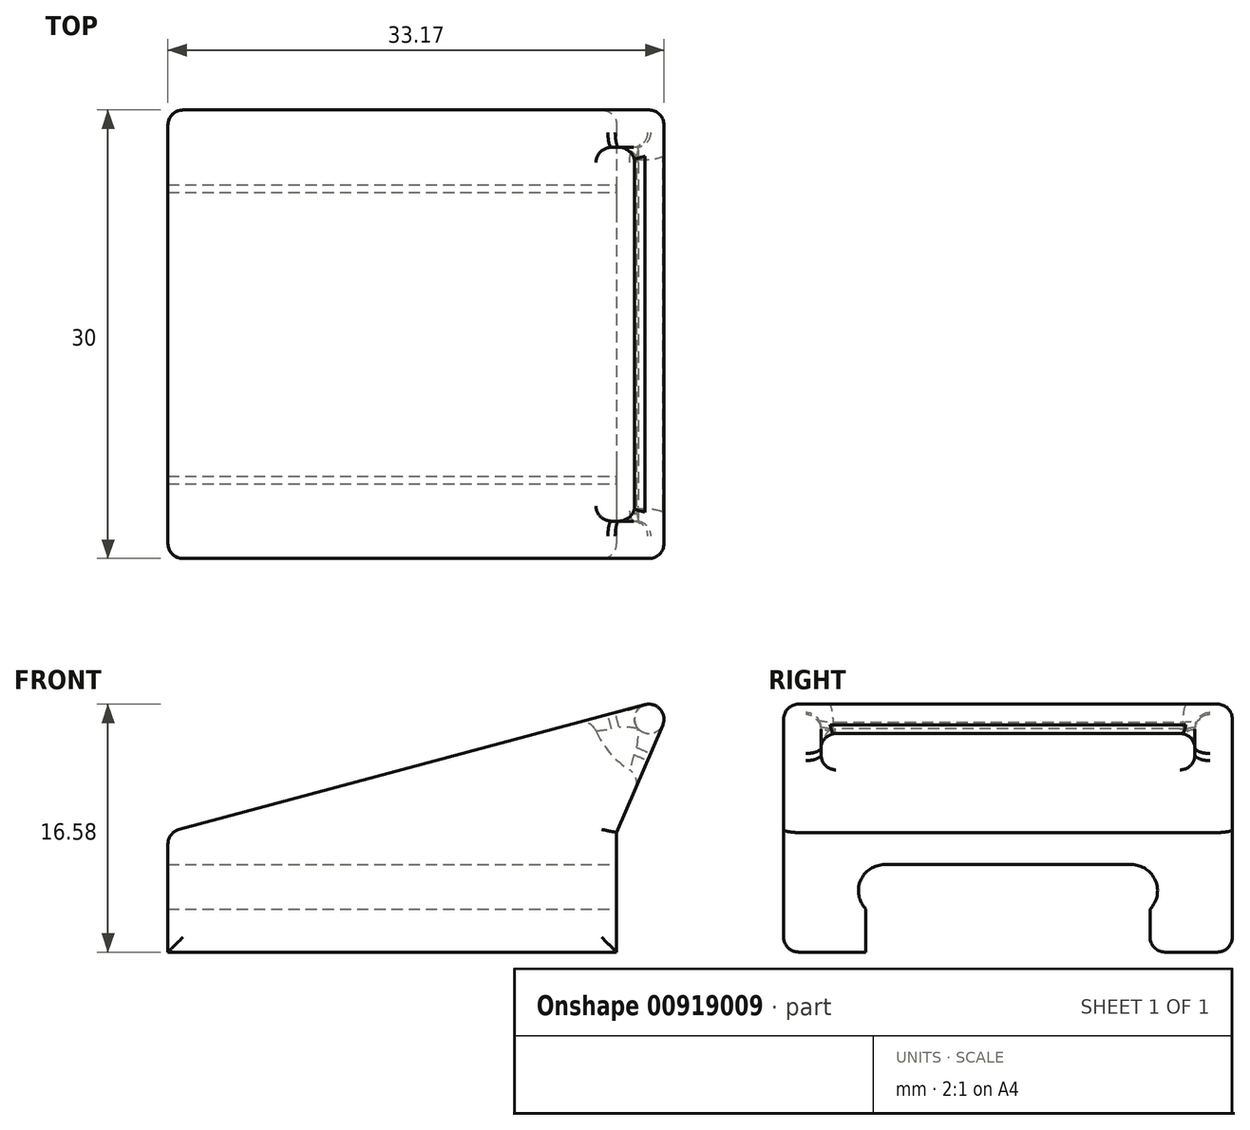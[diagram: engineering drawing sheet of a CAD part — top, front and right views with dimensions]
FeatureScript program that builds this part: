
annotation { "Feature Type Name" : "Feature", "Feature Type Description" : "" }
export const myFeature = defineFeature(function(context is Context, id is Id, definition is map)
    precondition{}
    {
        {
            var Q0;
            Q0=qCreatedBy(makeId("Top.planeOp"),FACE);
            var sketch = newSketch(context, id + "F0", { "sketchPlane" : qUnion([Q0])});
            skLineSegment(sketch, "E0.bottom", {"start": v(15, 15) * mm, "end": v(-15, 15) * mm});
            skLineSegment(sketch, "E0.top", {"start": v(15, -15) * mm, "end": v(-15, -15) * mm});
            skLineSegment(sketch, "E0.left", {"start": v(15, 15) * mm, "end": v(15, -15) * mm});
            skLineSegment(sketch, "E0.right", {"start": v(-15, 15) * mm, "end": v(-15, -15) * mm});
            skPoint(sketch, "E0.middle", {"position": v(0, 0) * mm});
            skSolve(sketch);
        }
        {
            var Q0;
            Q0=makeQuery(id+"F0.imprint","IMPRINT",FACE,{"disambiguationData":[TD([[makeQuery(id+"F0.imprint","IMPRINT",EDGE,{"derivedFrom":sQuery(id+"F0.wireOp",EDGE,"E0.bottom")}),1.0]])]});
            extrude(context, id + "F1", {"entities" : qUnion([Q0]), "oppositeDirection" : true, "depth" : 8 * mm, "offsetDistance" : 25 * mm});
        }
        {
            var Q0;
            Q0=makeQuery(id+"F1.opExtrude","SWEPT_FACE",FACE,{"disambiguationData":[OSD([sQuery(id+"F0.wireOp",EDGE,"E0.left")])]});
            var sketch = newSketch(context, id + "F2", { "sketchPlane" : qUnion([Q0])});
            skLineSegment(sketch, "E1", {"start": v(0, 9) * mm, "end": v(0, -16.8) * mm, "construction": true});
            skPoint(sketch, "E1.startSnap0", {"position": v(0, 0) * mm});
            skLineSegment(sketch, "E2.bottom", {"start": v(8.25, -2.15) * mm, "end": v(-8.25, -2.15) * mm});
            skLineSegment(sketch, "E2.left", {"start": v(10, -3.9) * mm, "end": v(10, -3.9) * mm});
            skLineSegment(sketch, "E2.right", {"start": v(-10, -3.9) * mm, "end": v(-10, -3.9) * mm});
            skPoint(sketch, "E2.middle", {"position": v(0, -3.9) * mm});
            skPoint(sketch, "E3.visualSharp", {"position": v(-10, -2.15) * mm});
            skArc(sketch, "E3.filletArc", {"start": v(-8.25, -2.15) * mm, "mid": v(-9.49, -2.66) * mm, "end": v(-10, -3.9) * mm});
            skPoint(sketch, "E4.visualSharp", {"position": v(-10, -5.65) * mm});
            skArc(sketch, "E4.filletArc", {"start": v(-10, -3.9) * mm, "mid": v(-9.87, -4.56) * mm, "end": v(-9.5, -5.12) * mm});
            skPoint(sketch, "E5.visualSharp", {"position": v(10, -5.65) * mm});
            skArc(sketch, "E5.filletArc", {"start": v(9.5, -5.12) * mm, "mid": v(9.87, -4.56) * mm, "end": v(10, -3.9) * mm});
            skPoint(sketch, "E6.visualSharp", {"position": v(10, -2.15) * mm});
            skArc(sketch, "E6.filletArc", {"start": v(10, -3.9) * mm, "mid": v(9.49, -2.66) * mm, "end": v(8.25, -2.15) * mm});
            skLineSegment(sketch, "E7", {"start": v(-9.5, -5.12) * mm, "end": v(-9.5, -8) * mm});
            skLineSegment(sketch, "E8", {"start": v(-9.5, -8) * mm, "end": v(9.5, -8) * mm});
            skLineSegment(sketch, "E9", {"start": v(9.5, -8) * mm, "end": v(9.5, -5.12) * mm});
            skSolve(sketch);
        }
        {
            var Q0;
            Q0=makeQuery(id+"F2.imprint","IMPRINT",FACE,{"disambiguationData":[TD([[makeQuery(id+"F2.imprint","IMPRINT",EDGE,{"derivedFrom":sQuery(id+"F2.wireOp",EDGE,"E2.bottom")}),1.0]])]});
            extrude(context, id + "F3", {"entities" : qUnion([Q0]), "operationType" : NewBodyOperationType.REMOVE, "endBound" : BoundingType.THROUGH_ALL, "oppositeDirection" : true, "depth" : 25 * mm, "offsetDistance" : 25 * mm});
        }
        {
            var Q0;
            Q0=makeQuery(id+"F1.opExtrude","SWEPT_FACE",FACE,{"disambiguationData":[OSD([sQuery(id+"F0.wireOp",EDGE,"E0.bottom")])]});
            var sketch = newSketch(context, id + "F4", { "sketchPlane" : qUnion([Q0])});
            skLineSegment(sketch, "E10.0", {"start": v(-15, 0) * mm, "end": v(15, 0) * mm});
            skLineSegment(sketch, "E11", {"start": v(-15, 0) * mm, "end": v(-18.9, 9.08) * mm});
            skLineSegment(sketch, "E12", {"start": v(-18.9, 9.08) * mm, "end": v(15, 0) * mm});
            skSolve(sketch);
        }
        {
            var Q0;
            Q0=makeQuery(id+"F4.imprint","IMPRINT",FACE,{"disambiguationData":[TD([[makeQuery(id+"F4.imprint","IMPRINT",EDGE,{"derivedFrom":sQuery(id+"F4.wireOp",EDGE,"E10.0")}),1.0]])]});
            extrude(context, id + "F5", {"entities" : qUnion([Q0]), "operationType" : NewBodyOperationType.ADD, "oppositeDirection" : true, "depth" : 30 * mm, "offsetDistance" : 25 * mm});
        }
        {
            var Q0;
            Q0=makeQuery(id+"F5.opExtrude","SWEPT_FACE",FACE,{"disambiguationData":[OSD([sQuery(id+"F4.wireOp",EDGE,"E11")])]});
            var sketch = newSketch(context, id + "F6", { "sketchPlane" : qUnion([Q0])});
            skLineSegment(sketch, "E13.bottom", {"start": v(11.5, 12.55) * mm, "end": v(-11.5, 12.55) * mm});
            skLineSegment(sketch, "E13.top", {"start": v(11.5, 10.05) * mm, "end": v(-11.5, 10.05) * mm});
            skLineSegment(sketch, "E13.left", {"start": v(12.5, 11.55) * mm, "end": v(12.5, 11.05) * mm});
            skLineSegment(sketch, "E13.right", {"start": v(-12.5, 11.55) * mm, "end": v(-12.5, 11.05) * mm});
            skPoint(sketch, "E13.middle", {"position": v(0, 11.3) * mm});
            skPoint(sketch, "E13.middle.positionSnap0", {"position": v(0, 15.8) * mm});
            skPoint(sketch, "E13.centerSnap0", {"position": v(0, 15.8) * mm});
            skPoint(sketch, "E14.visualSharp", {"position": v(-12.5, 12.55) * mm});
            skArc(sketch, "E14.filletArc", {"start": v(-11.5, 12.55) * mm, "mid": v(-12.2, 12.26) * mm, "end": v(-12.5, 11.55) * mm});
            skPoint(sketch, "E15.visualSharp", {"position": v(-12.5, 10.05) * mm});
            skArc(sketch, "E15.filletArc", {"start": v(-12.5, 11.05) * mm, "mid": v(-12.2, 10.34) * mm, "end": v(-11.5, 10.05) * mm});
            skPoint(sketch, "E16.visualSharp", {"position": v(12.5, 10.05) * mm});
            skArc(sketch, "E16.filletArc", {"start": v(11.5, 10.05) * mm, "mid": v(12.2, 10.34) * mm, "end": v(12.5, 11.05) * mm});
            skPoint(sketch, "E17.visualSharp", {"position": v(12.5, 12.55) * mm});
            skArc(sketch, "E17.filletArc", {"start": v(12.5, 11.55) * mm, "mid": v(12.2, 12.26) * mm, "end": v(11.5, 12.55) * mm});
            skSolve(sketch);
        }
        {
            var Q0;
            Q0=makeQuery(id+"F6.imprint","IMPRINT",FACE,{"disambiguationData":[TD([[makeQuery(id+"F6.imprint","IMPRINT",EDGE,{"derivedFrom":sQuery(id+"F6.wireOp",EDGE,"E13.bottom")}),1.0]])]});
            var Q1;
            Q1=makeQuery(id+"F5.opExtrude","SWEPT_EDGE",EDGE,{"disambiguationData":[OSD([sQuery(id+"F4.wireOp",EDGE,"E11"),sQuery(id+"F4.wireOp",EDGE,"E12")])]});
            revolve(context, id + "F7", {"operationType" : NewBodyOperationType.REMOVE, "surfaceOperationType" : NewSurfaceOperationType.NEW, "entities" : qUnion([Q0]), "axis" : qUnion([Q1]), "revolveType" : RevolveType.FULL, "oppositeDirection" : true});
        }
        {
            var Q0;
            Q0=makeQuery(id+"F5.opExtrude","SWEPT_EDGE",EDGE,{"disambiguationData":[OSD([sQuery(id+"F4.wireOp",EDGE,"E11"),sQuery(id+"F4.wireOp",EDGE,"E12")])]});
            var Q1;
            Q1=makeQuery(id+"F5.opExtrude","CAP_EDGE",EDGE,{"disambiguationData":[OSD([sQuery(id+"F4.wireOp",EDGE,"E12")])],"isStart":true});
            var Q2;
            Q2=makeQuery(id+"F5.opExtrude","CAP_EDGE",EDGE,{"disambiguationData":[OSD([sQuery(id+"F4.wireOp",EDGE,"E12")])],"isStart":false});
            var Q3;
            Q3=makeQuery(id+"F5.opExtrude","CAP_EDGE",EDGE,{"disambiguationData":[OSD([sQuery(id+"F4.wireOp",EDGE,"E11")])],"isStart":true});
            var Q4;
            Q4=makeQuery(id+"F1.opExtrude","SWEPT_EDGE",EDGE,{"disambiguationData":[OSD([sQuery(id+"F0.wireOp",EDGE,"E0.bottom"),sQuery(id+"F0.wireOp",EDGE,"E0.left")])]});
            var Q5;
            Q5=makeQuery(id+"F1.opExtrude","SWEPT_EDGE",EDGE,{"disambiguationData":[OSD([sQuery(id+"F0.wireOp",EDGE,"E0.top"),sQuery(id+"F0.wireOp",EDGE,"E0.left")])]});
            var Q6;
            Q6=makeQuery(id+"F5.opExtrude","CAP_EDGE",EDGE,{"disambiguationData":[OSD([sQuery(id+"F4.wireOp",EDGE,"E11")])],"isStart":false});
            var Q7;
            Q7=makeQuery(id+"F1.opExtrude","SWEPT_EDGE",EDGE,{"disambiguationData":[OSD([sQuery(id+"F0.wireOp",EDGE,"E0.top"),sQuery(id+"F0.wireOp",EDGE,"E0.right")])]});
            var Q8;
            Q8=makeQuery(id+"F1.opExtrude","SWEPT_EDGE",EDGE,{"disambiguationData":[OSD([sQuery(id+"F0.wireOp",EDGE,"E0.bottom"),sQuery(id+"F0.wireOp",EDGE,"E0.right")])]});
            var Q9;
            {var subQ0=sQuery(id+"F0.wireOp",EDGE,"E0.right");Q9=makeQuery(id+"F5.boolean.opBoolean","MERGE",EDGE,{"derivedFrom":[makeQuery(id+"F1.opExtrude","CAP_EDGE",EDGE,{"disambiguationData":[OSD([subQ0])],"isStart":true}),makeQuery(id+"F5.opExtrude","SWEPT_EDGE",EDGE,{"disambiguationData":[OSD([sQuery(id+"F0.wireOp",EDGE,"E0.bottom"),subQ0,sQuery(id+"F4.wireOp",EDGE,"E10.0"),sQuery(id+"F4.wireOp",EDGE,"E12")])]})]});}
            var Q10;
            Q10=makeQuery(id+"F3.boolean.opBoolean","COPY",EDGE,{"derivedFrom":makeQuery(id+"F3.opExtrude","SWEPT_EDGE",EDGE,{"disambiguationData":[OSD([sQuery(id+"F0.wireOp",EDGE,"E0.left"),sQuery(id+"F2.wireOp",EDGE,"E7"),sQuery(id+"F2.wireOp",EDGE,"E8")])]})});
            var Q11;
            Q11=makeQuery(id+"F3.boolean.opBoolean","COPY",EDGE,{"derivedFrom":makeQuery(id+"F3.opExtrude","SWEPT_EDGE",EDGE,{"disambiguationData":[OSD([sQuery(id+"F0.wireOp",EDGE,"E0.left"),sQuery(id+"F2.wireOp",EDGE,"E8"),sQuery(id+"F2.wireOp",EDGE,"E9")])]})});
            var Q12;
            Q12=makeQuery(id+"F1.opExtrude","CAP_EDGE",EDGE,{"disambiguationData":[OSD([sQuery(id+"F0.wireOp",EDGE,"E0.top")])],"isStart":false});
            var Q13;
            Q13=makeQuery(id+"F1.opExtrude","CAP_EDGE",EDGE,{"disambiguationData":[OSD([sQuery(id+"F0.wireOp",EDGE,"E0.bottom")])],"isStart":false});
            fillet(context, id + "F8", {"entities" : qUnion([Q0, Q1, Q2, Q3, Q4, Q5, Q6, Q7, Q8, Q9, Q10, Q11, Q12, Q13]), "radius" : 1 * mm, "tangentPropagation" : true, "allowEdgeOverflow" : false});
        }
        {
            var Q0;
            Q0=makeQuery(id+"F7.boolean.opBoolean","INTERSECT",EDGE,{"derivedFrom":[makeQuery(id+"F5.opExtrude","SWEPT_FACE",FACE,{"disambiguationData":[OSD([sQuery(id+"F4.wireOp",EDGE,"E12")])]}),makeQuery(id+"F7.opRevolve","SWEPT_FACE",FACE,{"disambiguationData":[OSD([sQuery(id+"F6.wireOp",EDGE,"E13.top")])]})]});
            var Q1;
            Q1=makeQuery(id+"F7.boolean.opBoolean","INTERSECT",EDGE,{"derivedFrom":[makeQuery(id+"F5.opExtrude","SWEPT_FACE",FACE,{"disambiguationData":[OSD([sQuery(id+"F4.wireOp",EDGE,"E11")])]}),makeQuery(id+"F7.opRevolve","SWEPT_FACE",FACE,{"disambiguationData":[OSD([sQuery(id+"F6.wireOp",EDGE,"E13.top")])]})]});
            fillet(context, id + "F9", {"entities" : qUnion([Q0, Q1]), "radius" : 1 * mm, "tangentPropagation" : true, "allowEdgeOverflow" : false});
        }
    });
